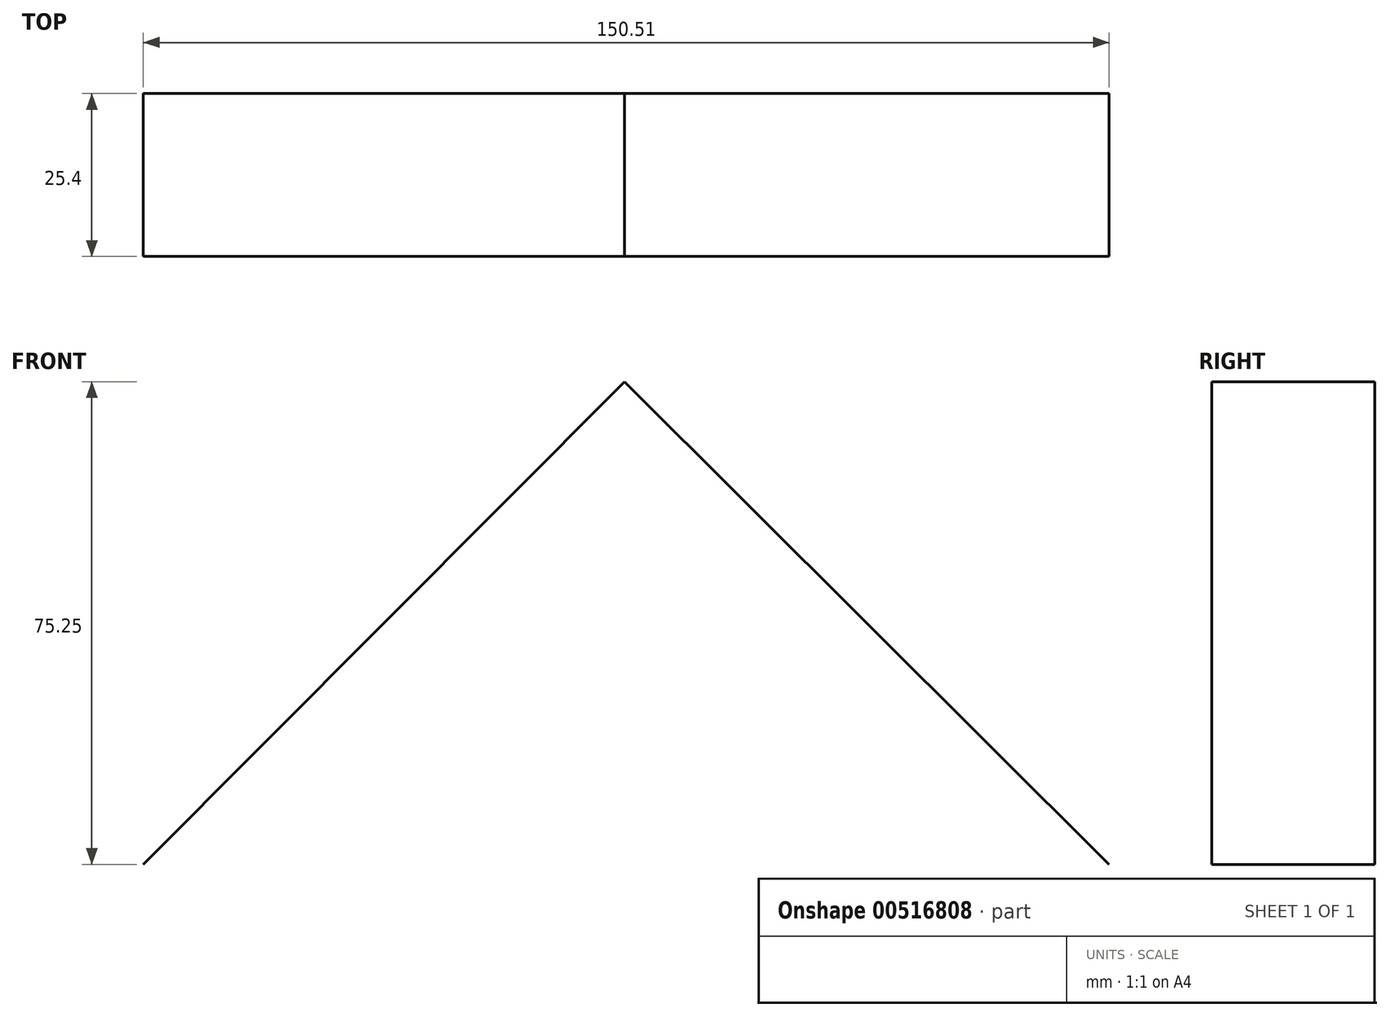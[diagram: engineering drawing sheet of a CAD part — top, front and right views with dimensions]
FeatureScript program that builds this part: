
annotation { "Feature Type Name" : "Feature", "Feature Type Description" : "" }
export const myFeature = defineFeature(function(context is Context, id is Id, definition is map)
    precondition{}
    {
        {
            var Q0;
            Q0=qCreatedBy(makeId("Front.planeOp"),FACE);
            var sketch = newSketch(context, id + "F0", { "sketchPlane" : qUnion([Q0])});
            skLineSegment(sketch, "E0", {"start": v(-76.1, 75.81) * mm, "end": v(75.53, -75.25) * mm});
            skLineSegment(sketch, "E1", {"start": v(75.53, -75.25) * mm, "end": v(0, 0) * mm});
            skLineSegment(sketch, "E2", {"start": v(0, 0) * mm, "end": v(75.53, 75.81) * mm});
            skLineSegment(sketch, "E3", {"start": v(75.53, 75.81) * mm, "end": v(-74.98, -75.25) * mm});
            skLineSegment(sketch, "E4", {"start": v(-74.98, -75.25) * mm, "end": v(0, 0) * mm});
            skLineSegment(sketch, "E5", {"start": v(0, 75.53) * mm, "end": v(0, -75.25) * mm});
            skLineSegment(sketch, "E6", {"start": v(0, -75.25) * mm, "end": v(0, 0) * mm});
            skLineSegment(sketch, "E7", {"start": v(75.53, 0) * mm, "end": v(-74.98, 0) * mm});
            skLineSegment(sketch, "E8", {"start": v(-74.98, 0) * mm, "end": v(0, 0) * mm});
            skSolve(sketch);
        }
        {
            var Q0;
            {var subQ0=sQuery(id+"F0.wireOp",EDGE,"E1");var subQ1=sQuery(id+"F0.wireOp",EDGE,"E0");var subQ2=makeQuery(id+"F0.imprint","INTERSECT",VERTEX,{"derivedFrom":[subQ1,subQ0]});Q0=makeQuery(id+"F0.imprint","IMPRINT",FACE,{"disambiguationData":[TD([[makeQuery(id+"F0.imprint","IMPRINT",EDGE,{"disambiguationData":[TD([[subQ2,1.0]])],"derivedFrom":subQ1}),-1.0]])]});}
            var Q1;
            {var subQ0=sQuery(id+"F0.wireOp",EDGE,"E4");Q1=makeQuery(id+"F0.imprint","IMPRINT",FACE,{"disambiguationData":[TD([[makeQuery(id+"F0.imprint","IMPRINT",EDGE,{"derivedFrom":subQ0}),1.0]])]});}
            var Q2;
            {var subQ0=sQuery(id+"F0.wireOp",EDGE,"E7");var subQ1=sQuery(id+"F0.wireOp",EDGE,"E0");var subQ2=makeQuery(id+"F0.imprint","INTERSECT",VERTEX,{"derivedFrom":[subQ1,subQ0]});Q2=makeQuery(id+"F0.imprint","IMPRINT",FACE,{"disambiguationData":[TD([[makeQuery(id+"F0.imprint","IMPRINT",EDGE,{"disambiguationData":[TD([[subQ2,1.0]])],"derivedFrom":subQ1}),-1.0]])]});}
            var Q3;
            {var subQ0=sQuery(id+"F0.wireOp",EDGE,"E8");var subQ1=sQuery(id+"F0.wireOp",EDGE,"E3");var subQ2=makeQuery(id+"F0.imprint","INTERSECT",VERTEX,{"derivedFrom":[subQ1,subQ0]});Q3=makeQuery(id+"F0.imprint","IMPRINT",FACE,{"disambiguationData":[TD([[makeQuery(id+"F0.imprint","IMPRINT",EDGE,{"disambiguationData":[TD([[subQ2,1.0]])],"derivedFrom":subQ1}),1.0]])]});}
            var Q4;
            {var subQ0=sQuery(id+"F0.wireOp",EDGE,"E2");var subQ1=sQuery(id+"F0.wireOp",EDGE,"E0");var subQ2=makeQuery(id+"F0.imprint","INTERSECT",VERTEX,{"derivedFrom":[subQ1,subQ0]});Q4=makeQuery(id+"F0.imprint","IMPRINT",FACE,{"disambiguationData":[TD([[makeQuery(id+"F0.imprint","IMPRINT",EDGE,{"disambiguationData":[TD([[subQ2,1.0]])],"derivedFrom":subQ1}),-1.0]])]});}
            extrude(context, id + "F1", {"entities" : qUnion([Q0, Q1, Q2, Q3, Q4]), "depth" : 25.4 * mm, "offsetDistance" : 25.4 * mm});
        }
    });
